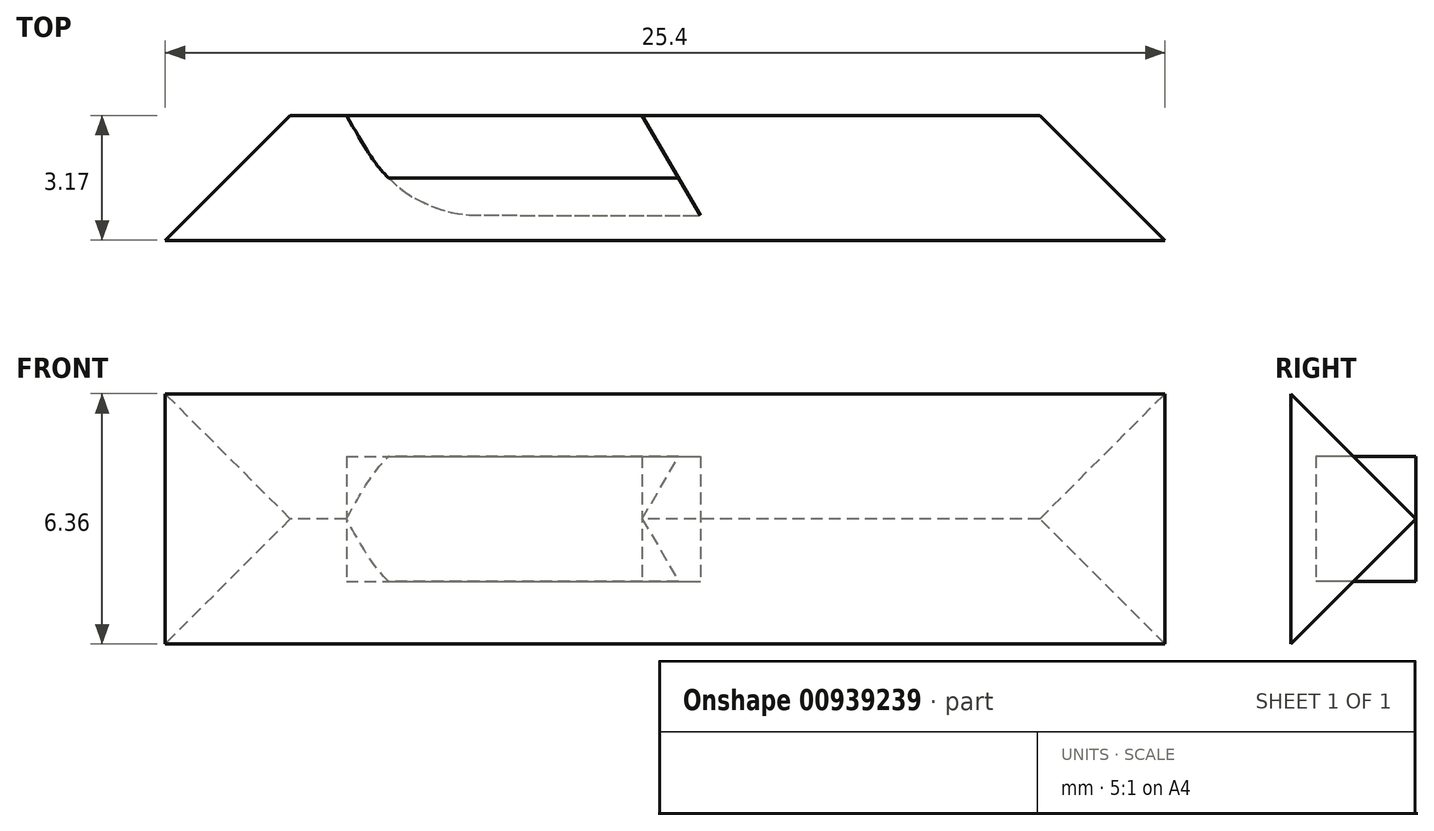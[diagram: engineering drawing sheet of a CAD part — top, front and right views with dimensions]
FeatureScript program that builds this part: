
annotation { "Feature Type Name" : "Feature", "Feature Type Description" : "" }
export const myFeature = defineFeature(function(context is Context, id is Id, definition is map)
    precondition{}
    {
        {
            var Q0;
            Q0=qCreatedBy(makeId("Top.planeOp"),FACE);
            var sketch = newSketch(context, id + "F0", { "sketchPlane" : qUnion([Q0])});
            skPoint(sketch, "E0", {"position": v(0, 11.87) * mm});
            skFitSpline(sketch, "E1", {"points": [v(-5.5, 11.87) * mm, v(5.63, 11.87) * mm], "startDerivative": vector(11.13, 0) * mm, "endDerivative": vector(11.13, 0) * mm});
            skFitSpline(sketch, "E2", {"points": [v(-12.18, 2.23) * mm, v(-12.28, 2.04) * mm, v(-12.42, 1.78) * mm, v(-12.6, 1.25) * mm, v(-12.7, 0.75) * mm, v(-12.7, 0.3) * mm, v(-12.63, -0.29) * mm, v(-12.51, -0.68) * mm, v(-12.34, -1.07) * mm, v(-11.7, -2.18) * mm, v(-11.08, -3.27) * mm, v(-9.33, -6.3) * mm, v(-7.43, -9.58) * mm, v(-7.2, -9.87) * mm, v(-7.02, -10.06) * mm, v(-6.82, -10.24) * mm, v(-6.64, -10.38) * mm, v(-6.43, -10.52) * mm, v(-6.04, -10.72) * mm, v(-5.87, -10.79) * mm, v(-5.5, -10.9) * mm, v(-5.14, -10.97) * mm, v(-4.95, -10.99) * mm, v(-4.88, -11) * mm, v(0.9, -11) * mm], "startDerivative": vector(-4, -7.78) * mm, "endDerivative": vector(65.54, -0.02) * mm});
            skFitSpline(sketch, "E3", {"points": [v(-12.18, 2.23) * mm, v(-7.86, 9.7) * mm, v(-7.74, 9.91) * mm, v(-7.6, 10.17) * mm, v(-7.44, 10.43) * mm, v(-7.24, 10.7) * mm, v(-6.99, 10.97) * mm, v(-6.74, 11.18) * mm, v(-6.6, 11.28) * mm, v(-6.45, 11.39) * mm, v(-6.31, 11.46) * mm, v(-6.15, 11.55) * mm, v(-6.04, 11.6) * mm, v(-5.9, 11.66) * mm, v(-5.64, 11.75) * mm, v(-5.4, 11.8) * mm, v(-5.16, 11.85) * mm, v(-4.95, 11.87) * mm, v(4.72, 11.87) * mm, v(5.08, 11.87) * mm, v(5.27, 11.84) * mm, v(5.51, 11.79) * mm, v(5.84, 11.68) * mm, v(6.06, 11.6) * mm, v(6.54, 11.33) * mm, v(6.82, 11.12) * mm, v(7.07, 10.88) * mm, v(7.26, 10.67) * mm, v(7.4, 10.48) * mm], "startDerivative": vector(38.81, 67.04) * mm, "endDerivative": vector(5, -8) * mm});
            skFitSpline(sketch, "E4", {"points": [v(7.4, 10.48) * mm, v(7.48, 10.35) * mm, v(12.33, 1.98) * mm, v(12.39, 1.86) * mm, v(12.45, 1.72) * mm, v(12.51, 1.54) * mm, v(12.58, 1.35) * mm, v(12.63, 1.15) * mm, v(12.66, 0.95) * mm, v(12.69, 0.73) * mm, v(12.7, 0.48) * mm, v(12.69, 0.19) * mm, v(12.65, -0.15) * mm, v(12.6, -0.36) * mm, v(12.55, -0.57) * mm, v(12.46, -0.8) * mm, v(12.36, -1.03) * mm, v(12.21, -1.28) * mm, v(11.57, -2.3) * mm, v(11, -3.23) * mm, v(10.88, -3.4) * mm, v(10.71, -3.61) * mm, v(10.5, -3.84) * mm, v(10.28, -4.03) * mm, v(10.04, -4.2) * mm, v(9.85, -4.32) * mm, v(9.79, -4.35) * mm, v(9.52, -4.49) * mm, v(9.21, -4.6) * mm, v(9, -4.66) * mm, v(8.64, -4.72) * mm, v(8.58, -4.73) * mm], "startDerivative": vector(1.47, -1.58) * mm, "endDerivative": vector(-3.39, -0.45) * mm});
            skLineSegment(sketch, "E5", {"start": v(2.6, -4.75) * mm, "end": v(8.4, -4.75) * mm});
            skFitSpline(sketch, "E6", {"points": [v(8.4, -4.75) * mm, v(8.49, -4.75) * mm, v(8.58, -4.73) * mm], "startDerivative": vector(0.18, 0) * mm, "endDerivative": vector(0.19, 0.04) * mm});
            skFitSpline(sketch, "E7", {"points": [v(2.6, -4.75) * mm, v(5.68, 0.44) * mm], "startDerivative": vector(3.07, 5.2) * mm, "endDerivative": vector(3.07, 5.2) * mm});
            skFitSpline(sketch, "E8", {"points": [v(5.68, 0.44) * mm, v(2.84, 5.36) * mm], "startDerivative": vector(-2.84, 4.92) * mm, "endDerivative": vector(-2.84, 4.92) * mm});
            skFitSpline(sketch, "E9", {"points": [v(2.84, 5.36) * mm, v(-2.84, 5.36) * mm], "startDerivative": vector(-5.67, 0) * mm, "endDerivative": vector(-5.67, 0) * mm});
            skFitSpline(sketch, "E10", {"points": [v(-2.84, 5.36) * mm, v(-5.68, 0.45) * mm], "startDerivative": vector(-2.84, -4.92) * mm, "endDerivative": vector(-2.84, -4.92) * mm});
            skFitSpline(sketch, "E11", {"points": [v(-5.68, 0.45) * mm, v(-5.68, 0.43) * mm, v(0.9, -11) * mm], "startDerivative": vector(-0.13, -0.33) * mm, "endDerivative": vector(10.13, -17.33) * mm});
            skLineSegment(sketch, "E12.bottom", {"start": v(-12.7, -8.46) * mm, "end": v(12.7, -8.46) * mm});
            skLineSegment(sketch, "E12.top", {"start": v(-12.7, -11.63) * mm, "end": v(12.7, -11.63) * mm});
            skLineSegment(sketch, "E12.left", {"start": v(-12.7, -8.46) * mm, "end": v(-12.7, -11.63) * mm});
            skLineSegment(sketch, "E12.right", {"start": v(12.7, -8.46) * mm, "end": v(12.7, -11.63) * mm});
            skSolve(sketch);
        }
        {
            var Q0;
            Q0=makeQuery(id+"F0.imprint","IMPRINT",FACE,{"disambiguationData":[TD([[makeQuery(id+"F0.imprint","IMPRINT",EDGE,{"derivedFrom":sQuery(id+"F0.wireOp",EDGE,"E12.top")}),1.0]])]});
            var Q1;
            {var subQ0=sQuery(id+"F0.wireOp",EDGE,"E11");var subQ1=sQuery(id+"F0.wireOp",EDGE,"E2");var subQ2=makeQuery(id+"F0.imprint","INTERSECT",VERTEX,{"derivedFrom":[subQ1,subQ0]});Q1=makeQuery(id+"F0.imprint","IMPRINT",FACE,{"disambiguationData":[TD([[makeQuery(id+"F0.imprint","IMPRINT",EDGE,{"disambiguationData":[TD([[subQ2,1.0]])],"derivedFrom":subQ1}),1.0]])]});}
            extrude(context, id + "F1", {"entities" : qUnion([Q0, Q1]), "depth" : 6.35 * mm, "offsetDistance" : 25.4 * mm, "symmetric" : true});
        }
        {
            var Q0;
            {var subQ7=sQuery(id+"F0.wireOp",EDGE,"E2");Q0=makeQuery(id+"F0.imprint","IMPRINT",FACE,{"disambiguationData":[TD([[makeQuery(id+"F0.imprint","IMPRINT",EDGE,{"derivedFrom":subQ7}),1.0]])]});}
            extrude(context, id + "F2", {"entities" : qUnion([Q0]), "operationType" : NewBodyOperationType.REMOVE, "depth" : 3.17 * mm, "offsetDistance" : 25.4 * mm, "symmetric" : true});
        }
        {
            var Q0;
            {var subQ0=sQuery(id+"F0.wireOp",EDGE,"E4");Q0=makeQuery(id+"F0.imprint","IMPRINT",FACE,{"disambiguationData":[TD([[makeQuery(id+"F0.imprint","IMPRINT",EDGE,{"derivedFrom":subQ0}),-1.0]])]});}
            var Q1;
            {var subQ0=sQuery(id+"F0.wireOp",EDGE,"E11");var subQ1=sQuery(id+"F0.wireOp",EDGE,"E2");var subQ2=makeQuery(id+"F0.imprint","INTERSECT",VERTEX,{"derivedFrom":[subQ1,subQ0]});Q1=makeQuery(id+"F0.imprint","IMPRINT",FACE,{"disambiguationData":[TD([[makeQuery(id+"F0.imprint","IMPRINT",EDGE,{"disambiguationData":[TD([[subQ2,1.0]])],"derivedFrom":subQ1}),1.0]])]});}
            extrude(context, id + "F3", {"entities" : qUnion([Q0, Q1]), "depth" : 3.17 * mm, "offsetDistance" : 25.4 * mm, "symmetric" : true});
        }
        {
            var Q0;
            Q0=makeQuery(id+"F1.opExtrude","SWEPT_EDGE",EDGE,{"disambiguationData":[OSD([sQuery(id+"F0.wireOp",EDGE,"E12.bottom"),sQuery(id+"F0.wireOp",EDGE,"E12.left")])]});
            var Q1;
            Q1=makeQuery(id+"F1.opExtrude","CAP_EDGE",EDGE,{"disambiguationData":[OSD([sQuery(id+"F0.wireOp",EDGE,"E12.bottom")])],"isStart":false});
            var Q2;
            Q2=makeQuery(id+"F1.opExtrude","CAP_EDGE",EDGE,{"disambiguationData":[OSD([sQuery(id+"F0.wireOp",EDGE,"E12.bottom")])],"isStart":true});
            var Q3;
            Q3=makeQuery(id+"F1.opExtrude","SWEPT_EDGE",EDGE,{"disambiguationData":[OSD([sQuery(id+"F0.wireOp",EDGE,"E12.bottom"),sQuery(id+"F0.wireOp",EDGE,"E12.right")])]});
            chamfer(context, id + "F4", {"entities" : qUnion([Q0, Q1, Q2, Q3]), "width" : 3.17 * mm, "tangentPropagation" : true});
        }
    });
